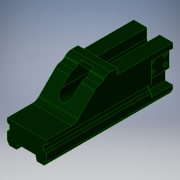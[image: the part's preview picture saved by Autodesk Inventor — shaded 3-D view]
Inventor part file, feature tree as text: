
AUTODESK INVENTOR PART (.ipt)
format: ipt  version: 2019 (Build 230136000, 136)  size: 293,888 bytes
history: native  units: mm
features: extrude x11, sketch x11, projected_geometry x3, chamfer x2, mirror x1, fillet x1
ambient origin geometry x8: Origin, YZ Plane, XZ Plane, XY Plane, X Axis, Y Axis, Z Axis, Center Point
bodies: Solid1 (feature_tree)
feature tree (29):
  extrude  "Extrusion1"  Depth=35.0mm
  extrude  "Extrusion2"  Depth=3.0mm
  extrude  "Extrusion3"  Depth=17.25mm TaperAngle=0.0deg
  mirror  "Mirror1"
  extrude  "Extrusion5"  Depth=15.0mm
  extrude  "Extrusion6"  Depth=6.0mm
  extrude  "Extrusion9"  Depth=10.0mm
  extrude  "Extrusion10"  Depth=7.5mm
  extrude  "Extrusion11"  Depth=10.0mm TaperAngle=0.0deg
  chamfer  "Chamfer4"  Distance=7.5mm
  extrude  "Extrusion12"  Depth=18.0mm TaperAngle=0.0deg
  chamfer  "Chamfer5"  Distance=2.0mm
  fillet  "Fillet1"  Radius=1.0mm
  extrude  "Extrusion13"  Depth=4.0mm
  extrude  "Extrusion14"  Depth=3.0mm TaperAngle=0.0deg
  sketch  "Sketch1"  dims[d0=31.0mm d1=35.0mm]
  sketch  "Sketch2"  dims[d2=30.0deg d3=3.0mm]
  sketch  "Sketch3"  dims[d4=60.0mm d5=0.0mm d8=17.25mm d9=0.0mm]
  projected_geometry  "Projected Loop1"
  sketch  "Sketch8"  dims[d11=10.0mm d12=15.0mm]
  sketch  "Sketch10"  dims[d13=3.0mm d14=6.0mm]
  sketch  "Sketch13"  dims[d16=10.0mm d20=3.2mm]
  projected_geometry  "Projected Loop3"
  sketch  "Sketch14"  dims[d21=8.5mm d22=0.0mm d51=7.5mm]
  sketch  "Sketch15"  dims[d52=10.0mm d53=10.0mm d54=0.0mm]
  sketch  "Sketch16"  dims[d60=10.0mm d61=7.5mm d62=0.0mm]
  sketch  "Sketch17"  dims[d73=18.0mm d74=40.0mm d75=0.0mm]
  sketch  "Sketch18"  dims[d76=6.0mm d77=2.0mm d78=1.0mm d79=4.0mm d80=115.0mm d81=0.0mm d83=16.0mm d84=8.0mm d85=4.5mm d86=10.0mm d87=0.0mm d94=17.0mm d95=2.0mm d96=45.0deg d97=12.0mm d98=8.0mm d99=2.0mm d100=2.0mm d101=95.0mm d102=0.0mm d103=4.5mm d104=2.0mm d105=45.0deg d106=7.0mm d108=6.0mm d109=0.0mm d111=2.7mm d112=10.0mm d113=0.0mm d114=19.0mm d115=3.05mm d116=4.0mm d117=4.0mm d119=4.0mm d120=3.0mm]
  projected_geometry  "Projected Loop5"
